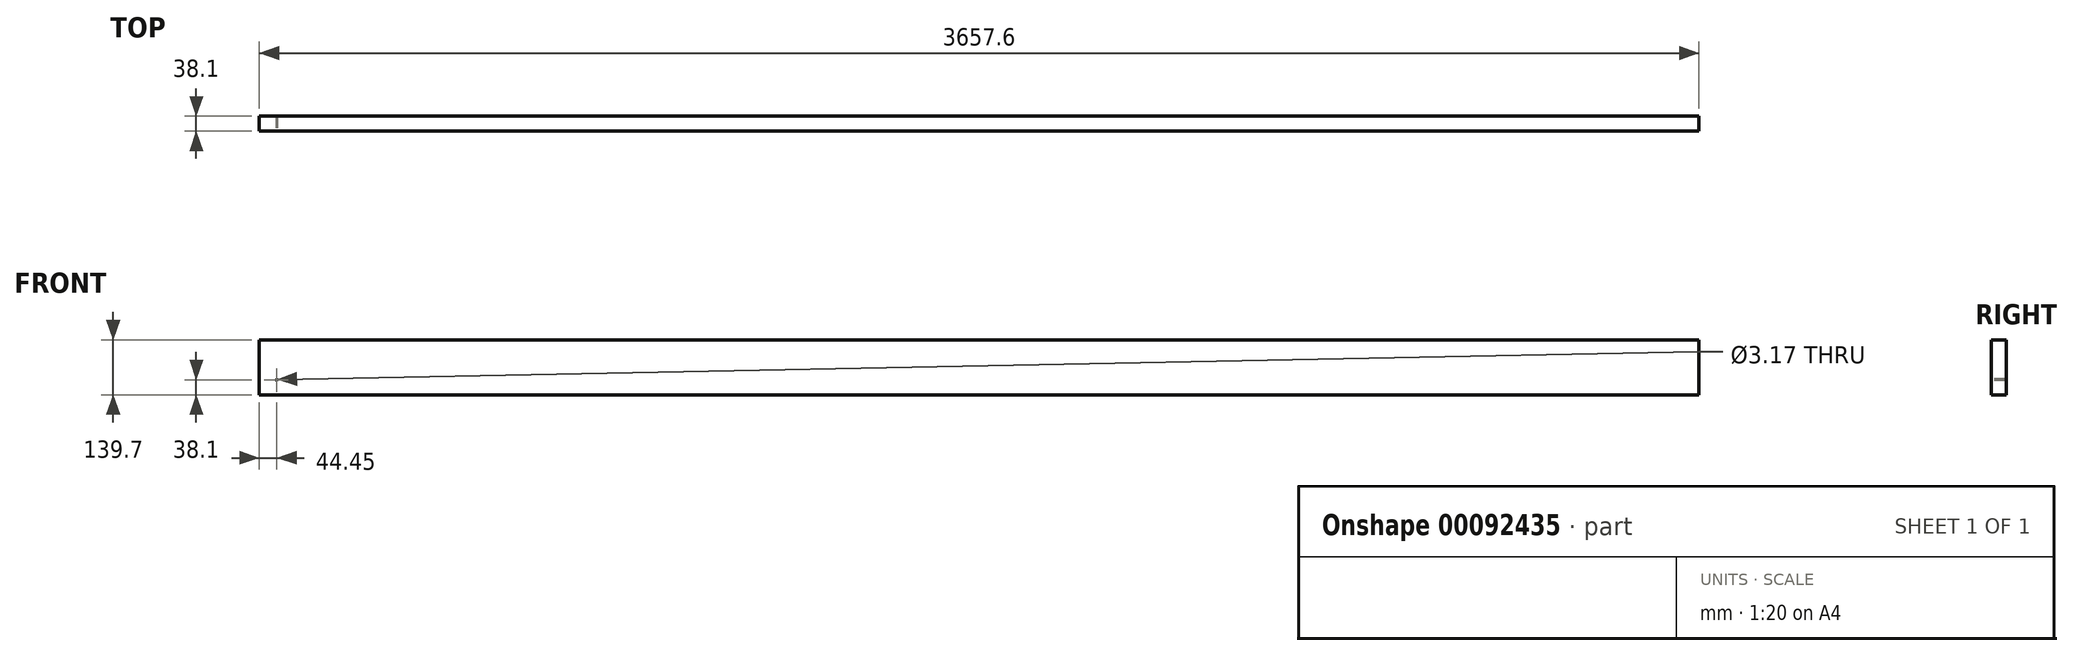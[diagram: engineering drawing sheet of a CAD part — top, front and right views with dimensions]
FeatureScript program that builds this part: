
annotation { "Feature Type Name" : "Feature", "Feature Type Description" : "" }
export const myFeature = defineFeature(function(context is Context, id is Id, definition is map)
    precondition{}
    {
        {
            var Q0;
            Q0=qCreatedBy(makeId("Right.planeOp"),FACE);
            var sketch = newSketch(context, id + "F0", { "sketchPlane" : qUnion([Q0])});
            skLineSegment(sketch, "E0.bottom", {"start": v(0, 0) * mm, "end": v(38.1, 0) * mm});
            skLineSegment(sketch, "E0.top", {"start": v(0, 139.7) * mm, "end": v(38.1, 139.7) * mm});
            skLineSegment(sketch, "E0.left", {"start": v(0, 0) * mm, "end": v(0, 139.7) * mm});
            skLineSegment(sketch, "E0.right", {"start": v(38.1, 0) * mm, "end": v(38.1, 139.7) * mm});
            skSolve(sketch);
        }
        {
            var Q0;
            Q0 = qSketchRegion(id + "F0", true);
            extrude(context, id + "F1", {"entities" : qUnion([Q0]), "depth" : 3657.6 * mm});
        }
        {
            var Q0;
            Q0=makeQuery(id+"F1.opExtrude","SWEPT_FACE",FACE,{"disambiguationData":[OSD([sQuery(id+"F0.wireOp",EDGE,"E0.left")])]});
            var sketch = newSketch(context, id + "F2", { "sketchPlane" : qUnion([Q0])});
            skCircle(sketch, "E1", {"center": v(44.45, 38.1) * mm, "radius": 1.59 * mm});
            skSolve(sketch);
        }
        {
            var Q0;
            Q0 = qSketchRegion(id + "F2", true);
            extrude(context, id + "F3", {"entities" : qUnion([Q0]), "operationType" : NewBodyOperationType.REMOVE, "endBound" : BoundingType.UP_TO_NEXT, "oppositeDirection" : true, "depth" : 25.4 * mm});
        }
    });
